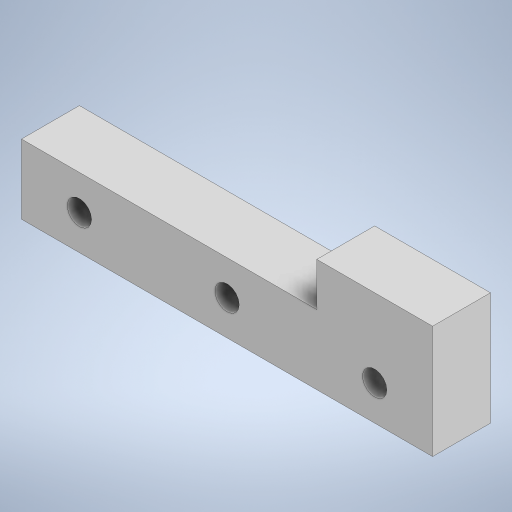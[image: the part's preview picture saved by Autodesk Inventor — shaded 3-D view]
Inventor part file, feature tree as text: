
AUTODESK INVENTOR PART (.ipt)
format: ipt  version: 2023 (Build 270158000, 158)  size: 257,024 bytes
history: native  units: in
note: dims shown in document units (in); Inventor stores cm internally (conversion verified against a paired STEP export)
features: extrude x1, sketch x1
ambient origin geometry x8: Origin, YZ Plane, XZ Plane, XY Plane, X Axis, Y Axis, Z Axis, Center Point
bodies: Solid1 (feature_tree)
feature tree (2):
  extrude  "Extrusion1"  Depth=0.4724in
  sketch  "Sketch1"  dims[d0=2.7953in d1=0.4724in d2=0.3937in d3=0.2362in d4=0.3937in d5=0.2362in d6=0.2362in d7=1.3976in d8=0.1654in d9=0.1654in d10=0.1654in d11=0.7874in d12=0.2953in d13=0.3937in d14=0.0in]
